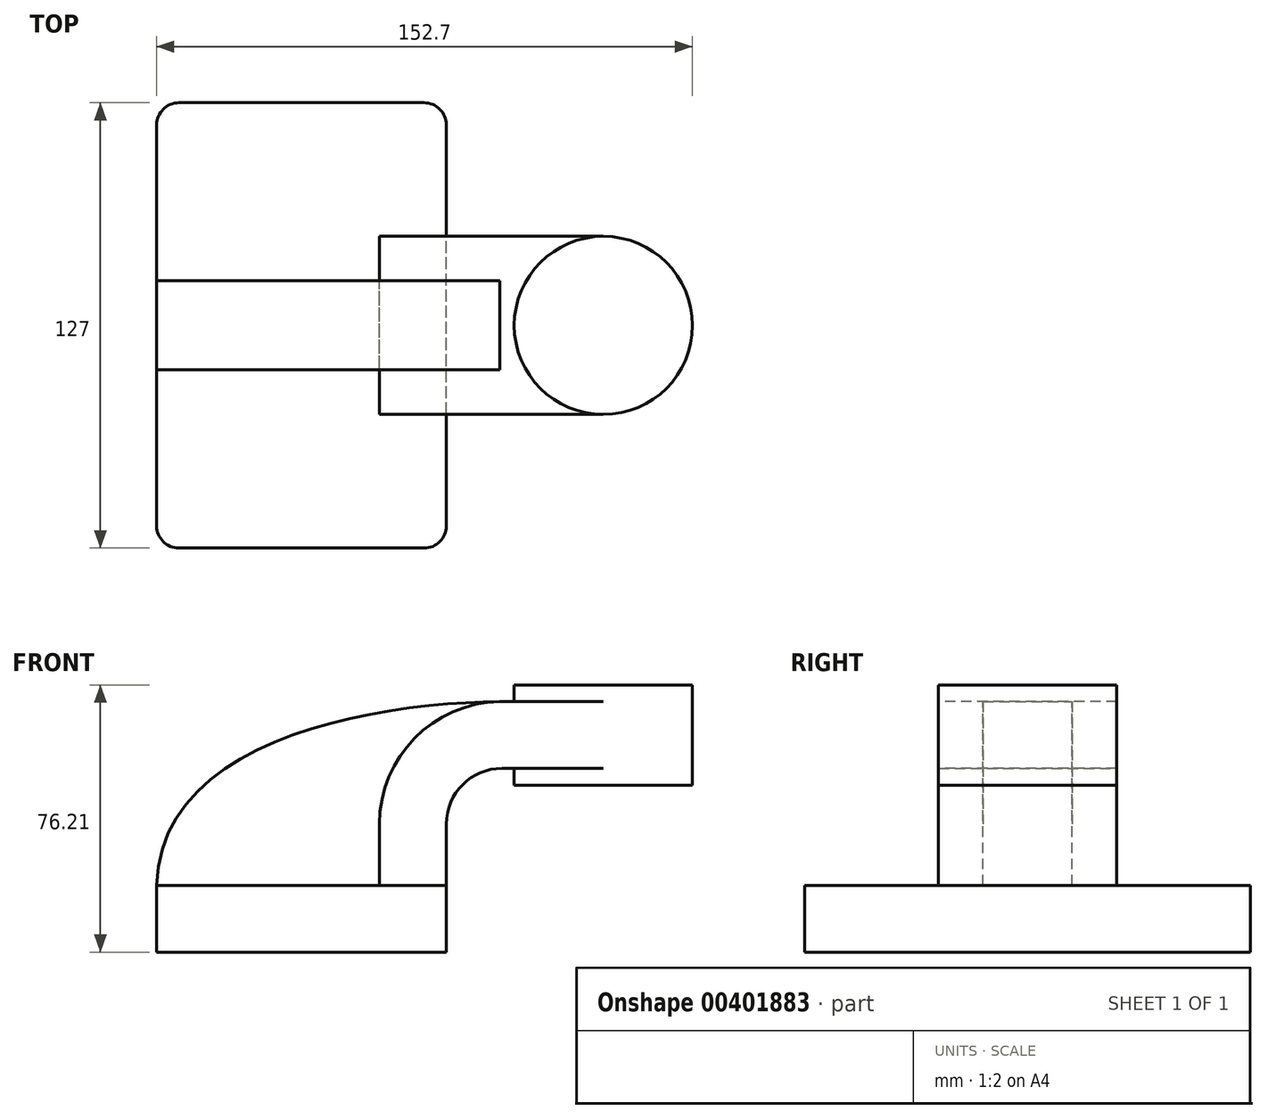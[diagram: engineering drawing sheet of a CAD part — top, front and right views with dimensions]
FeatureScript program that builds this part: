
annotation { "Feature Type Name" : "Feature", "Feature Type Description" : "" }
export const myFeature = defineFeature(function(context is Context, id is Id, definition is map)
    precondition{}
    {
        {
            var Q0;
            Q0=qCreatedBy(makeId("Front.planeOp"),FACE);
            var sketch = newSketch(context, id + "F0", { "sketchPlane" : qUnion([Q0])});
            skLineSegment(sketch, "E0.bottom", {"start": v(41.27, 9.53) * mm, "end": v(-41.28, 9.53) * mm});
            skLineSegment(sketch, "E0.top", {"start": v(41.28, -9.52) * mm, "end": v(-41.27, -9.52) * mm});
            skLineSegment(sketch, "E0.left", {"start": v(41.28, 9.53) * mm, "end": v(41.28, -9.52) * mm});
            skLineSegment(sketch, "E0.right", {"start": v(-41.28, 9.53) * mm, "end": v(-41.27, -9.52) * mm});
            skPoint(sketch, "E0.middle", {"position": v(0, 0) * mm});
            skLineSegment(sketch, "E1.bottom", {"start": v(60.62, 66.68) * mm, "end": v(111.42, 66.68) * mm});
            skLineSegment(sketch, "E1.top", {"start": v(60.62, 38.1) * mm, "end": v(111.42, 38.1) * mm});
            skLineSegment(sketch, "E1.left", {"start": v(60.62, 66.68) * mm, "end": v(60.62, 38.1) * mm});
            skLineSegment(sketch, "E1.right", {"start": v(111.42, 66.68) * mm, "end": v(111.42, 38.1) * mm});
            skPoint(sketch, "E1.middle", {"position": v(86.02, 52.39) * mm});
            skLineSegment(sketch, "E2", {"start": v(41.27, 9.53) * mm, "end": v(41.27, 27) * mm});
            skArc(sketch, "E3", {"start": v(41.27, 27) * mm, "mid": v(45.92, 38.23) * mm, "end": v(57.15, 42.88) * mm});
            skLineSegment(sketch, "E4", {"start": v(57.15, 42.88) * mm, "end": v(86.02, 42.88) * mm});
            skLineSegment(sketch, "E5.0", {"start": v(57.15, 61.93) * mm, "end": v(86.02, 61.93) * mm});
            skArc(sketch, "E5.1", {"start": v(22.23, 27) * mm, "mid": v(32.45, 51.7) * mm, "end": v(57.15, 61.93) * mm});
            skLineSegment(sketch, "E5.2", {"start": v(22.22, 9.53) * mm, "end": v(22.22, 27) * mm});
            skFitSpline(sketch, "E6", {"points": [v(-41.28, 9.52) * mm, v(57.15, 61.93) * mm], "startDerivative": vector(3.55, 126.98) * mm, "endDerivative": vector(105.13, 0.76) * mm});
            skLineSegment(sketch, "E7", {"start": v(86.02, 61.93) * mm, "end": v(86.02, 42.88) * mm});
            skLineSegment(sketch, "E8", {"start": v(86.02, 61.93) * mm, "end": v(86.02, 66.68) * mm});
            skLineSegment(sketch, "E9", {"start": v(86.02, 42.88) * mm, "end": v(86.02, 38.1) * mm});
            skSolve(sketch);
        }
        {
            var Q0;
            Q0=makeQuery(id+"F0.imprint","IMPRINT",FACE,{"disambiguationData":[TD([[makeQuery(id+"F0.imprint","IMPRINT",EDGE,{"derivedFrom":sQuery(id+"F0.wireOp",EDGE,"E0.top")}),-1.0]])]});
            extrude(context, id + "F1", {"entities" : qUnion([Q0]), "endBound" : BoundingType.SYMMETRIC, "depth" : 127 * mm});
        }
        {
            var Q0;
            {var subQ1=sQuery(id+"F0.wireOp",EDGE,"E2");Q0=makeQuery(id+"F0.imprint","IMPRINT",FACE,{"disambiguationData":[TD([[makeQuery(id+"F0.imprint","IMPRINT",EDGE,{"derivedFrom":subQ1}),1.0]])]});}
            var Q1;
            {var subQ5=sQuery(id+"F0.wireOp",EDGE,"E7");Q1=makeQuery(id+"F0.imprint","IMPRINT",FACE,{"disambiguationData":[TD([[makeQuery(id+"F0.imprint","IMPRINT",EDGE,{"derivedFrom":subQ5}),-1.0]])]});}
            extrude(context, id + "F2", {"entities" : qUnion([Q0, Q1]), "endBound" : BoundingType.SYMMETRIC, "depth" : 50.8 * mm});
        }
        {
            var Q0;
            {var subQ3=sQuery(id+"F0.wireOp",EDGE,"E5.2");Q0=makeQuery(id+"F0.imprint","IMPRINT",FACE,{"disambiguationData":[TD([[makeQuery(id+"F0.imprint","IMPRINT",EDGE,{"derivedFrom":subQ3}),1.0]])]});}
            extrude(context, id + "F3", {"entities" : qUnion([Q0]), "endBound" : BoundingType.SYMMETRIC, "depth" : 25.4 * mm});
        }
        {
            var Q0;
            {var subQ0=sQuery(id+"F0.wireOp",EDGE,"E1.right");Q0=makeQuery(id+"F0.imprint","IMPRINT",FACE,{"disambiguationData":[TD([[makeQuery(id+"F0.imprint","IMPRINT",EDGE,{"derivedFrom":subQ0}),-1.0]])]});}
            var Q1;
            Q1=sQuery(id+"F0.wireOp",EDGE,"E7");
            revolve(context, id + "F4", {"operationType" : NewBodyOperationType.ADD, "entities" : qUnion([Q0]), "axis" : qUnion([Q1]), "revolveType" : RevolveType.FULL});
        }
        {
            var Q0;
            Q0=makeQuery(id+"F1.opExtrude","CAP_EDGE",EDGE,{"disambiguationData":[OSD([sQuery(id+"F0.wireOp",EDGE,"E0.left")])],"isStart":false});
            var Q1;
            Q1=makeQuery(id+"F1.opExtrude","CAP_EDGE",EDGE,{"disambiguationData":[OSD([sQuery(id+"F0.wireOp",EDGE,"E0.right")])],"isStart":false});
            var Q2;
            Q2=makeQuery(id+"F1.opExtrude","CAP_EDGE",EDGE,{"disambiguationData":[OSD([sQuery(id+"F0.wireOp",EDGE,"E0.left")])],"isStart":true});
            var Q3;
            Q3=makeQuery(id+"F1.opExtrude","CAP_EDGE",EDGE,{"disambiguationData":[OSD([sQuery(id+"F0.wireOp",EDGE,"E0.right")])],"isStart":true});
            fillet(context, id + "F5", {"entities" : qUnion([Q0, Q1, Q2, Q3]), "radius" : 6.35 * mm, "tangentPropagation" : true, "allowEdgeOverflow" : false});
        }
    });
